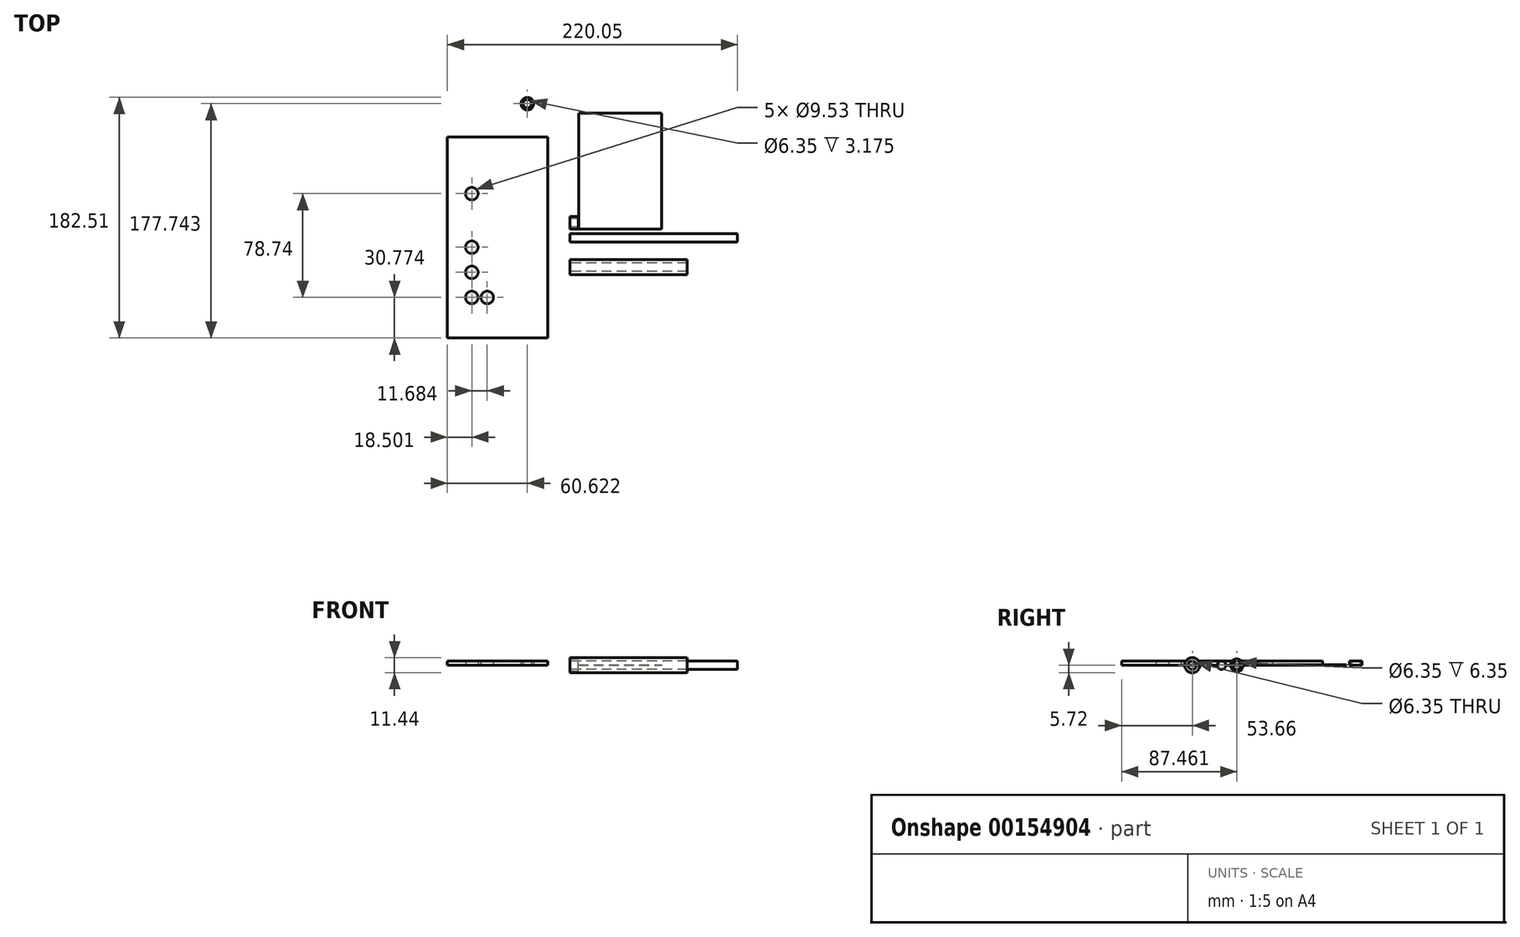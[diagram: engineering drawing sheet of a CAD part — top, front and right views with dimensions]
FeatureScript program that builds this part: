
annotation { "Feature Type Name" : "Feature", "Feature Type Description" : "" }
export const myFeature = defineFeature(function(context is Context, id is Id, definition is map)
    precondition{}
    {
        {
            var Q0;
            Q0=qCreatedBy(makeId("Right.planeOp"),FACE);
            var sketch = newSketch(context, id + "F0", { "sketchPlane" : qUnion([Q0])});
            skCircle(sketch, "E0", {"center": v(0, 0) * mm, "radius": 3.18 * mm});
            skCircle(sketch, "E1", {"center": v(11.61, 0) * mm, "radius": 4.76 * mm});
            skCircle(sketch, "E2", {"center": v(11.61, 0) * mm, "radius": 3.18 * mm});
            skCircle(sketch, "E3", {"center": v(-22.19, 0) * mm, "radius": 5.72 * mm});
            skCircle(sketch, "E4", {"center": v(-22.19, 0) * mm, "radius": 3.18 * mm});
            skSolve(sketch);
        }
        {
            var Q0;
            Q0=makeQuery(id+"F0.imprint","IMPRINT",FACE,{"disambiguationData":[TD([[makeQuery(id+"F0.imprint","IMPRINT",EDGE,{"derivedFrom":sQuery(id+"F0.wireOp",EDGE,"E0")}),1.0]])]});
            extrude(context, id + "F1", {"entities" : qUnion([Q0]), "depth" : 127 * mm});
        }
        {
            var Q0;
            Q0=makeQuery(id+"F0.imprint","IMPRINT",FACE,{"disambiguationData":[TD([[makeQuery(id+"F0.imprint","IMPRINT",EDGE,{"derivedFrom":sQuery(id+"F0.wireOp",EDGE,"E3")}),1.0]])]});
            extrude(context, id + "F2", {"entities" : qUnion([Q0]), "depth" : 88.9 * mm});
        }
        {
            var Q0;
            Q0=qCreatedBy(makeId("Top.planeOp"),FACE);
            var sketch = newSketch(context, id + "F3", { "sketchPlane" : qUnion([Q0])});
            skLineSegment(sketch, "E5.bottom", {"start": v(6.38, 6.93) * mm, "end": v(69.38, 6.93) * mm});
            skLineSegment(sketch, "E5.top", {"start": v(6.38, 94.87) * mm, "end": v(69.38, 94.87) * mm});
            skLineSegment(sketch, "E5.left", {"start": v(6.38, 6.93) * mm, "end": v(6.38, 94.87) * mm});
            skLineSegment(sketch, "E5.right", {"start": v(69.38, 6.93) * mm, "end": v(69.38, 94.87) * mm});
            skSolve(sketch);
        }
        {
            var Q0;
            Q0=makeQuery(id+"F3.imprint","IMPRINT",FACE,{"disambiguationData":[TD([[makeQuery(id+"F3.imprint","IMPRINT",EDGE,{"derivedFrom":sQuery(id+"F3.wireOp",EDGE,"E5.bottom")}),1.0]])]});
            extrude(context, id + "F4", {"entities" : qUnion([Q0]), "depth" : 0.3 * mm});
        }
        {
            var Q0;
            Q0=makeQuery(id+"F0.imprint","IMPRINT",FACE,{"disambiguationData":[TD([[makeQuery(id+"F0.imprint","IMPRINT",EDGE,{"derivedFrom":sQuery(id+"F0.wireOp",EDGE,"E1")}),1.0]])]});
            extrude(context, id + "F5", {"entities" : qUnion([Q0]), "depth" : 6.35 * mm});
        }
        {
            var Q0;
            Q0=qCreatedBy(makeId("Top.planeOp"),FACE);
            var sketch = newSketch(context, id + "F6", { "sketchPlane" : qUnion([Q0])});
            skLineSegment(sketch, "E6.0", {"start": v(-9.65, -75.85) * mm, "end": v(-6.48, -75.85) * mm});
            skLineSegment(sketch, "E7.0", {"start": v(-9.65, 76.55) * mm, "end": v(-6.48, 76.55) * mm});
            skLineSegment(sketch, "E8.bottom", {"start": v(-93.05, 76.55) * mm, "end": v(-16.85, 76.55) * mm});
            skLineSegment(sketch, "E8.top", {"start": v(-93.05, -75.85) * mm, "end": v(-16.85, -75.85) * mm});
            skLineSegment(sketch, "E8.left", {"start": v(-93.05, 76.55) * mm, "end": v(-93.05, -75.85) * mm});
            skLineSegment(sketch, "E8.right", {"start": v(-16.85, 76.55) * mm, "end": v(-16.85, -75.85) * mm});
            skCircle(sketch, "E9", {"center": v(-74.55, 33.66) * mm, "radius": 4.76 * mm});
            skCircle(sketch, "E10", {"center": v(-74.55, -6.98) * mm, "radius": 4.76 * mm});
            skLineSegment(sketch, "E11", {"start": v(-74.55, 33.66) * mm, "end": v(-74.55, -6.98) * mm, "construction": true});
            skLineSegment(sketch, "E12.bottom", {"start": v(-61.16, 37.4) * mm, "end": v(-39.15, 37.4) * mm, "construction": true});
            skLineSegment(sketch, "E12.top", {"start": v(-61.16, -25.6) * mm, "end": v(-39.15, -25.6) * mm, "construction": true});
            skLineSegment(sketch, "E12.left", {"start": v(-61.16, 37.4) * mm, "end": v(-61.16, -25.6) * mm, "construction": true});
            skLineSegment(sketch, "E12.right", {"start": v(-39.15, 37.4) * mm, "end": v(-39.15, -25.6) * mm, "construction": true});
            skCircle(sketch, "E13", {"center": v(-74.55, 33.66) * mm, "radius": 5.84 * mm, "construction": true});
            skCircle(sketch, "E14", {"center": v(-74.55, -6.98) * mm, "radius": 5.84 * mm, "construction": true});
            skLineSegment(sketch, "E15", {"start": v(-68.7, -6.98) * mm, "end": v(-68.7, 33.66) * mm, "construction": true});
            skLineSegment(sketch, "E16", {"start": v(-68.7, -6.98) * mm, "end": v(-68.7, -46.79) * mm, "construction": true});
            skLineSegment(sketch, "E17", {"start": v(-74.55, 33.66) * mm, "end": v(-68.7, 33.66) * mm, "construction": true});
            skLineSegment(sketch, "E18", {"start": v(-74.55, -6.98) * mm, "end": v(-68.7, -6.98) * mm, "construction": true});
            skLineSegment(sketch, "E19", {"start": v(-74.55, -6.98) * mm, "end": v(-74.55, -57.62) * mm, "construction": true});
            skCircle(sketch, "E20", {"center": v(-74.55, -45.08) * mm, "radius": 5.84 * mm, "construction": true});
            skLineSegment(sketch, "E21", {"start": v(-74.55, -45.08) * mm, "end": v(-68.7, -45.08) * mm, "construction": true});
            skCircle(sketch, "E22", {"center": v(-74.55, -45.08) * mm, "radius": 4.76 * mm});
            skLineSegment(sketch, "E23", {"start": v(-68.7, -45.08) * mm, "end": v(-62.87, -45.08) * mm, "construction": true});
            skCircle(sketch, "E24", {"center": v(-62.87, -45.08) * mm, "radius": 4.76 * mm});
            skCircle(sketch, "E25", {"center": v(-62.87, -45.08) * mm, "radius": 5.84 * mm, "construction": true});
            skPoint(sketch, "E26", {"position": v(-69.79, -45.08) * mm});
            skPoint(sketch, "E27", {"position": v(-67.63, -45.08) * mm});
            skCircle(sketch, "E28", {"center": v(-74.55, -26.01) * mm, "radius": 5.84 * mm, "construction": true});
            skCircle(sketch, "E29", {"center": v(-74.55, -26.01) * mm, "radius": 4.76 * mm});
            skSolve(sketch);
        }
        {
            var Q0;
            Q0=makeQuery(id+"F6.imprint","IMPRINT",FACE,{"disambiguationData":[TD([[makeQuery(id+"F6.imprint","IMPRINT",EDGE,{"derivedFrom":sQuery(id+"F6.wireOp",EDGE,"E8.bottom")}),-1.0]])]});
            extrude(context, id + "F7", {"entities" : qUnion([Q0]), "depth" : 3.17 * mm});
        }
        {
            var Q0;
            Q0=qCreatedBy(makeId("Top.planeOp"),FACE);
            var sketch = newSketch(context, id + "F8", { "sketchPlane" : qUnion([Q0])});
            skCircle(sketch, "E30", {"center": v(-32.43, 101.9) * mm, "radius": 3.18 * mm});
            skCircle(sketch, "E31", {"center": v(-32.43, 101.9) * mm, "radius": 4.76 * mm});
            skSolve(sketch);
        }
        {
            var Q0;
            Q0=makeQuery(id+"F8.imprint","IMPRINT",FACE,{"disambiguationData":[TD([[makeQuery(id+"F8.imprint","IMPRINT",EDGE,{"derivedFrom":sQuery(id+"F8.wireOp",EDGE,"E30")}),-1.0]])]});
            extrude(context, id + "F9", {"entities" : qUnion([Q0]), "depth" : 3.17 * mm});
        }
    });
